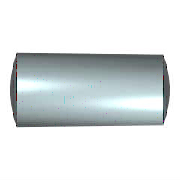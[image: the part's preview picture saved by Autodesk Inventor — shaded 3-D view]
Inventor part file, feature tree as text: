
AUTODESK INVENTOR PART (.ipt)
format: ipt  version: 2020 (Build 240168000, 168)  size: 116,224 bytes
history: native  units: mm (DEFAULTED — no unit token found)
features: other x1, sketch x1
ambient origin geometry x8: Origin, YZ Plane, XZ Plane, XY Plane, X Axis, Y Axis, Z Axis, Center Point
bodies: Solid1 (feature_tree)
feature tree (2):
  other  "轴承体"
  sketch  "草图1"  dims[d0=40.0mm d1=1.2mm d2=1.2mm d4=90.0deg d3=10.0mm d5=10.752mm d24=0.0mm d35=1.2mm d36=1.2mm]
